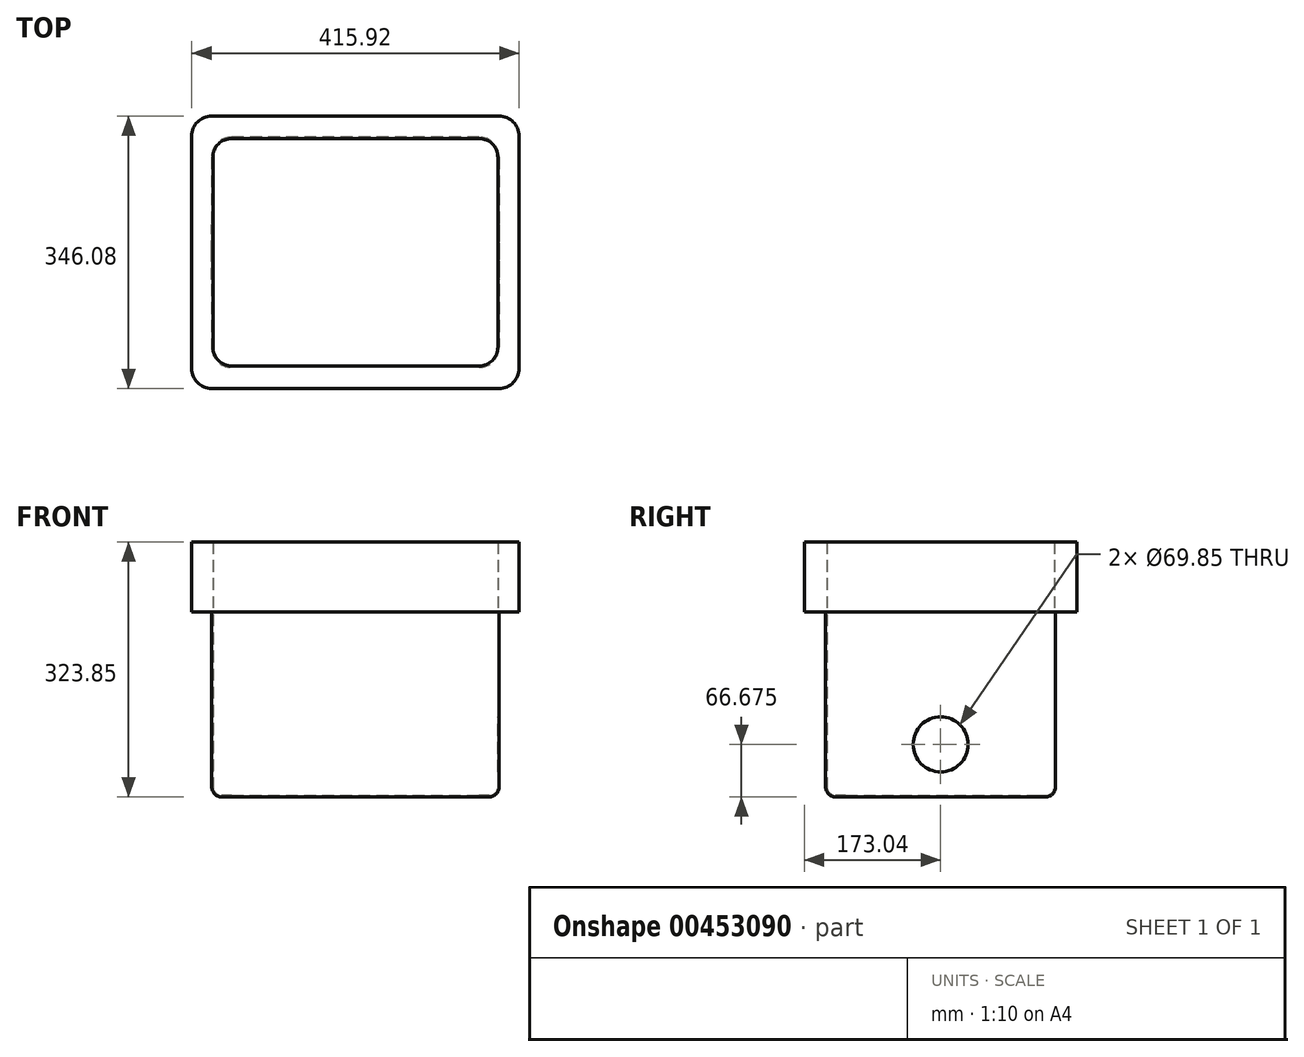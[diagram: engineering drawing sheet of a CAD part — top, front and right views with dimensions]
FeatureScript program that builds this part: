
annotation { "Feature Type Name" : "Feature", "Feature Type Description" : "" }
export const myFeature = defineFeature(function(context is Context, id is Id, definition is map)
    precondition{}
    {
        {
            var Q0;
            Q0=qCreatedBy(makeId("Top.planeOp"),FACE);
            var sketch = newSketch(context, id + "F0", { "sketchPlane" : qUnion([Q0])});
            skLineSegment(sketch, "E0.bottom", {"start": v(182.56, 146.05) * mm, "end": v(-182.56, 146.05) * mm});
            skLineSegment(sketch, "E0.top", {"start": v(182.56, -146.05) * mm, "end": v(-182.56, -146.05) * mm});
            skLineSegment(sketch, "E0.left", {"start": v(182.56, 146.05) * mm, "end": v(182.56, -146.05) * mm});
            skLineSegment(sketch, "E0.right", {"start": v(-182.56, 146.05) * mm, "end": v(-182.56, -146.05) * mm});
            skPoint(sketch, "E0.middle", {"position": v(0, 0) * mm});
            skSolve(sketch);
        }
        {
            var Q0;
            Q0 = qSketchRegion(id + "F0", true);
            extrude(context, id + "F1", {"entities" : qUnion([Q0]), "depth" : 323.85 * mm});
        }
        {
            var Q0;
            Q0=makeQuery(id+"F1.opExtrude","SWEPT_EDGE",EDGE,{"disambiguationData":[OSD([sQuery(id+"F0.wireOp",EDGE,"E0.top"),sQuery(id+"F0.wireOp",EDGE,"E0.right")])]});
            var Q1;
            Q1=makeQuery(id+"F1.opExtrude","SWEPT_EDGE",EDGE,{"disambiguationData":[OSD([sQuery(id+"F0.wireOp",EDGE,"E0.top"),sQuery(id+"F0.wireOp",EDGE,"E0.left")])]});
            var Q2;
            Q2=makeQuery(id+"F1.opExtrude","SWEPT_EDGE",EDGE,{"disambiguationData":[OSD([sQuery(id+"F0.wireOp",EDGE,"E0.bottom"),sQuery(id+"F0.wireOp",EDGE,"E0.left")])]});
            var Q3;
            Q3=makeQuery(id+"F1.opExtrude","SWEPT_EDGE",EDGE,{"disambiguationData":[OSD([sQuery(id+"F0.wireOp",EDGE,"E0.bottom"),sQuery(id+"F0.wireOp",EDGE,"E0.right")])]});
            fillet(context, id + "F2", {"entities" : qUnion([Q0, Q1, Q2, Q3]), "radius" : 25.4 * mm, "tangentPropagation" : true, "allowEdgeOverflow" : false});
        }
        {
            var Q0;
            Q0=makeQuery(id+"F1.opExtrude","CAP_EDGE",EDGE,{"disambiguationData":[OSD([sQuery(id+"F0.wireOp",EDGE,"E0.top")])],"isStart":true});
            fillet(context, id + "F3", {"entities" : qUnion([Q0]), "radius" : 12.7 * mm, "tangentPropagation" : true, "allowEdgeOverflow" : false});
        }
        {
            var Q0;
            Q0=makeQuery(id+"F1.opExtrude","CAP_FACE",FACE,{"disambiguationData":[OSD([sQuery(id+"F0.wireOp",EDGE,"E0.bottom"),sQuery(id+"F0.wireOp",EDGE,"E0.top"),sQuery(id+"F0.wireOp",EDGE,"E0.left"),sQuery(id+"F0.wireOp",EDGE,"E0.right")])],"isStart":false});
            shell(context, id + "F4", {"entities" : qUnion([Q0]), "thickness" : 1.59 * mm});
        }
        {
            var Q0;
            Q0=makeQuery(id+"F1.opExtrude","SWEPT_FACE",FACE,{"disambiguationData":[OSD([sQuery(id+"F0.wireOp",EDGE,"E0.left")])]});
            var sketch = newSketch(context, id + "F5", { "sketchPlane" : qUnion([Q0])});
            skLineSegment(sketch, "E1", {"start": v(0, 12.7) * mm, "end": v(0, 323.85) * mm, "construction": true});
            skCircle(sketch, "E2", {"center": v(0, 66.67) * mm, "radius": 34.93 * mm});
            skPoint(sketch, "E3", {"position": v(0, 101.6) * mm});
            skSolve(sketch);
        }
        {
            var Q0;
            Q0 = qSketchRegion(id + "F5", true);
            extrude(context, id + "F6", {"entities" : qUnion([Q0]), "operationType" : NewBodyOperationType.REMOVE, "endBound" : BoundingType.THROUGH_ALL, "oppositeDirection" : true, "depth" : 25.4 * mm, "offsetDistance" : 25.4 * mm});
        }
        {
            var Q0;
            Q0=makeQuery(id+"F1.opExtrude","CAP_FACE",FACE,{"disambiguationData":[OSD([sQuery(id+"F0.wireOp",EDGE,"E0.bottom"),sQuery(id+"F0.wireOp",EDGE,"E0.top"),sQuery(id+"F0.wireOp",EDGE,"E0.left"),sQuery(id+"F0.wireOp",EDGE,"E0.right")])],"isStart":false});
            var sketch = newSketch(context, id + "F7", { "sketchPlane" : qUnion([Q0])});
            skLineSegment(sketch, "E4.bottom", {"start": v(207.96, 173.04) * mm, "end": v(-207.96, 173.04) * mm});
            skLineSegment(sketch, "E4.top", {"start": v(207.96, -173.04) * mm, "end": v(-207.96, -173.04) * mm});
            skLineSegment(sketch, "E4.left", {"start": v(207.96, 173.04) * mm, "end": v(207.96, -173.04) * mm});
            skLineSegment(sketch, "E4.right", {"start": v(-207.96, 173.04) * mm, "end": v(-207.96, -173.04) * mm});
            skPoint(sketch, "E4.middle", {"position": v(0, 0) * mm});
            skLineSegment(sketch, "E5", {"start": v(-182.56, 120.65) * mm, "end": v(-182.56, -120.65) * mm});
            skLineSegment(sketch, "E6", {"start": v(-157.16, -146.05) * mm, "end": v(157.16, -146.05) * mm});
            skLineSegment(sketch, "E7", {"start": v(182.56, -120.65) * mm, "end": v(182.56, 120.65) * mm});
            skLineSegment(sketch, "E8", {"start": v(157.16, 146.05) * mm, "end": v(-157.16, 146.05) * mm});
            skArc(sketch, "E9", {"start": v(-157.16, 146.05) * mm, "mid": v(-175.12, 138.61) * mm, "end": v(-182.56, 120.65) * mm});
            skArc(sketch, "E10", {"start": v(-182.56, -120.65) * mm, "mid": v(-175.12, -138.61) * mm, "end": v(-157.16, -146.05) * mm});
            skArc(sketch, "E11", {"start": v(157.16, -146.05) * mm, "mid": v(175.12, -138.61) * mm, "end": v(182.56, -120.65) * mm});
            skArc(sketch, "E12", {"start": v(182.56, 120.65) * mm, "mid": v(175.12, 138.61) * mm, "end": v(157.16, 146.05) * mm});
            skSolve(sketch);
        }
        {
            var Q0;
            Q0 = qSketchRegion(id + "F7", true);
            extrude(context, id + "F8", {"entities" : qUnion([Q0]), "operationType" : NewBodyOperationType.ADD, "oppositeDirection" : true, "depth" : 88.9 * mm, "offsetDistance" : 25.4 * mm});
        }
        {
            var Q0;
            Q0=makeQuery(id+"F8.opExtrude","SWEPT_EDGE",EDGE,{"disambiguationData":[OSD([sQuery(id+"F7.wireOp",EDGE,"E4.top"),sQuery(id+"F7.wireOp",EDGE,"E4.right")])]});
            var Q1;
            Q1=makeQuery(id+"F8.opExtrude","SWEPT_EDGE",EDGE,{"disambiguationData":[OSD([sQuery(id+"F7.wireOp",EDGE,"E4.top"),sQuery(id+"F7.wireOp",EDGE,"E4.left")])]});
            var Q2;
            Q2=makeQuery(id+"F8.opExtrude","SWEPT_EDGE",EDGE,{"disambiguationData":[OSD([sQuery(id+"F7.wireOp",EDGE,"E4.bottom"),sQuery(id+"F7.wireOp",EDGE,"E4.left")])]});
            var Q3;
            Q3=makeQuery(id+"F8.opExtrude","SWEPT_EDGE",EDGE,{"disambiguationData":[OSD([sQuery(id+"F7.wireOp",EDGE,"E4.bottom"),sQuery(id+"F7.wireOp",EDGE,"E4.right")])]});
            fillet(context, id + "F9", {"entities" : qUnion([Q0, Q1, Q2, Q3]), "tangentPropagation" : true, "radius" : 25.4 * mm, "defaultsChanged" : true, "vertexSettings" : [], "allowEdgeOverflow" : false});
        }
    });
